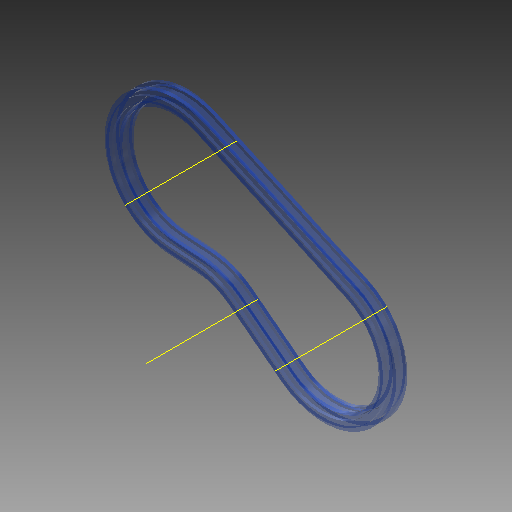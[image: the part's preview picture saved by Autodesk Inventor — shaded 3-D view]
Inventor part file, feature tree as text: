
AUTODESK INVENTOR PART (.ipt)
format: ipt  version: 2017 (Build 210142000, 142)  size: 226,816 bytes
history: native  units: mm
features: other x6, plane x2, pattern_linear x1
ambient origin geometry x8: Origin, YZ Plane, XZ Plane, XY Plane, X Axis, Y Axis, Z Axis, Center Point
bodies: Solid1 (feature_tree), Solid (feature_tree)
feature tree (9):
  other  "Work Axis1"
  other  "Work Axis2"
  other  "Work Axis3"
  plane  "Work Plane2"
  plane  "Work Plane3"
  other  "Path"
  other  "Section Plane"
  pattern_linear  "Strand Pattern"  Spacing1=0.0mm  [1 undecoded]
  other  "Section Sketch"
note: 1 required parameter value undecoded (feature->parameter linkage not recoverable at this tier; creation-order binding heuristic only, values carry confidence <= 0.55)
